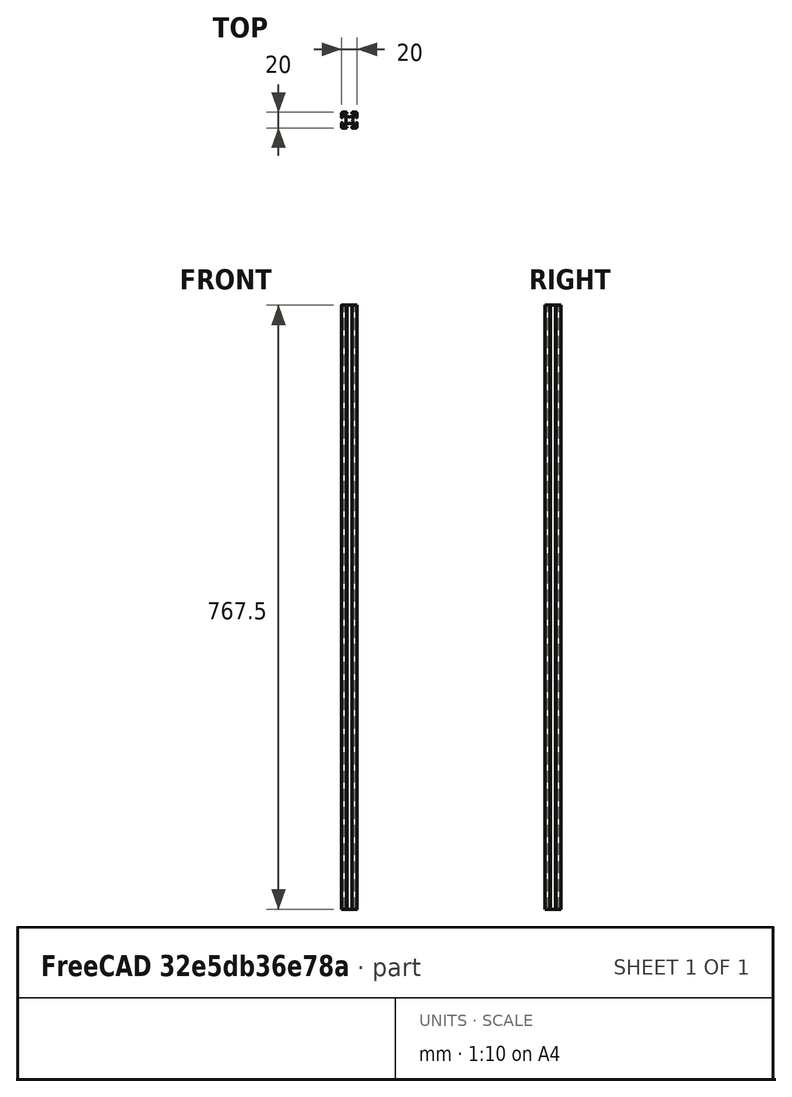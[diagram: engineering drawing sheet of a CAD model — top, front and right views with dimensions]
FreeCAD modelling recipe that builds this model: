
FCSTD DOCUMENT  (FreeCAD 0.15R4671 (Git))
Label: Perfil vertical 767.5 mm
License: CC-BY 3.0
LicenseURL: http://creativecommons.org/licenses/by/3.0/
objects: Sketcher::SketchObject×2, PartDesign::Pad×1, PartDesign::Pocket×1, Part::MultiFuse×1
note: 7 computed .brp shape members not serialized (recipe doc carries the construction recipe); baked Part::Feature solids carry a one-line shape summary decoded from their .brp

FEATURE [Sketcher::SketchObject] Sketch
  Placement = pos=(1.5,0,0) rot=(0,0,1;0rad)
  sketch-geometry (136):
    g0: LineSegment StartX=0 StartY=20 StartZ=0 EndX=4.65 EndY=20 EndZ=0
    g1: ArcOfCircle CenterX=-1e-12 CenterY=18.5 CenterZ=0 NormalX=0 NormalY=0 NormalZ=1 Radius=1.5 StartAngle=1.5708 EndAngle=3.14159
    g2: LineSegment StartX=-1.5 StartY=13.85 StartZ=0 EndX=-1.5 EndY=18.5 EndZ=0
    g3: ArcOfCircle CenterX=-1.3 CenterY=13.85 CenterZ=0 NormalX=0 NormalY=0 NormalZ=1 Radius=0.2 StartAngle=3.14159 EndAngle=4.71239
    g4: LineSegment StartX=-1 StartY=13.65 StartZ=0 EndX=-1.3 EndY=13.65 EndZ=0
    g5: LineSegment StartX=-1 StartY=13.3 StartZ=0 EndX=-1 EndY=13.65 EndZ=0
    g6: ArcOfCircle CenterX=-0.8 CenterY=13.3 CenterZ=0 NormalX=0 NormalY=0 NormalZ=1 Radius=0.2 StartAngle=3.14159 EndAngle=4.71239
    g7: LineSegment StartX=-0.5 StartY=13.1 StartZ=0 EndX=-0.8 EndY=13.1 EndZ=0
    g8: ArcOfCircle CenterX=-0.5 CenterY=13.6 CenterZ=0 NormalX=0 NormalY=0 NormalZ=1 Radius=0.5 StartAngle=4.71239 EndAngle=6.28319
    g9: LineSegment StartX=2.68e-07 StartY=15.5 StartZ=0 EndX=2.68e-07 EndY=13.6 EndZ=0
    g10: ArcOfCircle CenterX=0.5 CenterY=15.5 CenterZ=0 NormalX=0 NormalY=0 NormalZ=1 Radius=0.5 StartAngle=1.5708 EndAngle=3.14159
    g11: LineSegment StartX=1.23223 StartY=16 StartZ=0 EndX=0.5 EndY=16 EndZ=0
    g12: ArcOfCircle CenterX=1.23223 CenterY=15.5 CenterZ=0 NormalX=0 NormalY=0 NormalZ=1 Radius=0.5 StartAngle=0.785398 EndAngle=1.5708
    g13: LineSegment StartX=3.85355 StartY=13.5858 StartZ=0 EndX=1.58579 EndY=15.8536 EndZ=0
    g14: ArcOfCircle CenterX=3.5 CenterY=13.2322 CenterZ=0 NormalX=0 NormalY=0 NormalZ=1 Radius=0.5 StartAngle=0 EndAngle=0.785398
    g15: LineSegment StartX=4 StartY=10.9536 StartZ=0 EndX=4 EndY=13.2322 EndZ=0
    g16: ArcOfCircle CenterX=4.2 CenterY=10.9536 CenterZ=0 NormalX=0 NormalY=0 NormalZ=1 Radius=0.2 StartAngle=3.14159 EndAngle=3.66519
    g17: LineSegment StartX=4.46188 StartY=10.1 StartZ=0 EndX=4.0268 EndY=10.8536 EndZ=0
    g18: ArcOfCircle CenterX=4.28868 CenterY=10 CenterZ=0 NormalX=0 NormalY=0 NormalZ=1 Radius=0.2 StartAngle=5.75959 EndAngle=6.80678
    g19: LineSegment StartX=4.0268 StartY=9.14641 StartZ=0 EndX=4.46188 EndY=9.9 EndZ=0
    g20: ArcOfCircle CenterX=4.2 CenterY=9.04641 CenterZ=0 NormalX=0 NormalY=0 NormalZ=1 Radius=0.2 StartAngle=2.61799 EndAngle=3.14159
    g21: LineSegment StartX=4 StartY=6.76777 StartZ=0 EndX=4 EndY=9.04641 EndZ=0
    g22: ArcOfCircle CenterX=3.5 CenterY=6.76777 CenterZ=0 NormalX=0 NormalY=0 NormalZ=1 Radius=0.5 StartAngle=5.49779 EndAngle=6.28319
    g23: LineSegment StartX=1.58579 StartY=4.14645 StartZ=0 EndX=3.85355 EndY=6.41421 EndZ=0
    g24: ArcOfCircle CenterX=1.23223 CenterY=4.5 CenterZ=0 NormalX=0 NormalY=0 NormalZ=1 Radius=0.5 StartAngle=4.71239 EndAngle=5.49779
    g25: LineSegment StartX=0.5 StartY=4 StartZ=0 EndX=1.23223 EndY=4 EndZ=0
    g26: ArcOfCircle CenterX=0.5 CenterY=4.5 CenterZ=0 NormalX=0 NormalY=0 NormalZ=1 Radius=0.5 StartAngle=3.14159 EndAngle=4.71239
    g27: LineSegment StartX=2.68e-07 StartY=6.4 StartZ=0 EndX=2.68e-07 EndY=4.5 EndZ=0
    g28: ArcOfCircle CenterX=-0.5 CenterY=6.4 CenterZ=0 NormalX=0 NormalY=0 NormalZ=1 Radius=0.5 StartAngle=0 EndAngle=1.5708
    g29: LineSegment StartX=-0.8 StartY=6.9 StartZ=0 EndX=-0.5 EndY=6.9 EndZ=0
    g30: ArcOfCircle CenterX=-0.8 CenterY=6.7 CenterZ=0 NormalX=0 NormalY=0 NormalZ=1 Radius=0.2 StartAngle=1.5708 EndAngle=3.14159
    g31: LineSegment StartX=-1 StartY=6.35 StartZ=0 EndX=-1 EndY=6.7 EndZ=0
    g32: LineSegment StartX=-1.3 StartY=6.35 StartZ=0 EndX=-1 EndY=6.35 EndZ=0
    g33: ArcOfCircle CenterX=-1.3 CenterY=6.15 CenterZ=0 NormalX=0 NormalY=0 NormalZ=1 Radius=0.2 StartAngle=1.5708 EndAngle=3.14159
    g34: LineSegment StartX=-1.5 StartY=1.5 StartZ=0 EndX=-1.5 EndY=6.15 EndZ=0
    g35: ArcOfCircle CenterX=0 CenterY=1.5 CenterZ=0 NormalX=0 NormalY=0 NormalZ=1 Radius=1.5 StartAngle=3.14159 EndAngle=4.71239
    g36: LineSegment StartX=4.65 StartY=1e-12 StartZ=0 EndX=0 EndY=0 EndZ=0
    g37: ArcOfCircle CenterX=4.65 CenterY=0.2 CenterZ=0 NormalX=0 NormalY=0 NormalZ=1 Radius=0.2 StartAngle=4.71239 EndAngle=6.28319
    g38: LineSegment StartX=4.85 StartY=0.5 StartZ=0 EndX=4.85 EndY=0.2 EndZ=0
    g39: LineSegment StartX=5.2 StartY=0.5 StartZ=0 EndX=4.85 EndY=0.5 EndZ=0
    g40: ArcOfCircle CenterX=5.2 CenterY=0.7 CenterZ=0 NormalX=0 NormalY=0 NormalZ=1 Radius=0.2 StartAngle=4.71239 EndAngle=6.28319
    g41: LineSegment StartX=5.4 StartY=1 StartZ=0 EndX=5.4 EndY=0.7 EndZ=0
    g42: ArcOfCircle CenterX=4.9 CenterY=1 CenterZ=0 NormalX=0 NormalY=0 NormalZ=1 Radius=0.5 StartAngle=0 EndAngle=1.5708
    g43: LineSegment StartX=3 StartY=1.5 StartZ=0 EndX=4.9 EndY=1.5 EndZ=0
    g44: ArcOfCircle CenterX=3 CenterY=2 CenterZ=0 NormalX=0 NormalY=0 NormalZ=1 Radius=0.5 StartAngle=3.14159 EndAngle=4.71239
    g45: LineSegment StartX=2.5 StartY=2.73223 StartZ=0 EndX=2.5 EndY=2 EndZ=0
    g46: ArcOfCircle CenterX=3 CenterY=2.73223 CenterZ=0 NormalX=0 NormalY=0 NormalZ=1 Radius=0.5 StartAngle=2.35619 EndAngle=3.14159
    g47: LineSegment StartX=4.91421 StartY=5.35355 StartZ=0 EndX=2.64645 EndY=3.08579 EndZ=0
    g48: ArcOfCircle CenterX=5.26777 CenterY=5 CenterZ=0 NormalX=0 NormalY=0 NormalZ=1 Radius=0.5 StartAngle=1.5708 EndAngle=2.35619
    g49: LineSegment StartX=7.54641 StartY=5.5 StartZ=0 EndX=5.26777 EndY=5.5 EndZ=0
    g50: ArcOfCircle CenterX=7.54641 CenterY=5.7 CenterZ=0 NormalX=0 NormalY=0 NormalZ=1 Radius=0.2 StartAngle=4.71239 EndAngle=5.23599
    g51: LineSegment StartX=8.4 StartY=5.96188 StartZ=0 EndX=7.64641 EndY=5.52679 EndZ=0
    g52: ArcOfCircle CenterX=8.5 CenterY=5.78868 CenterZ=0 NormalX=0 NormalY=0 NormalZ=1 Radius=0.2 StartAngle=1.0472 EndAngle=2.0944
    g53: LineSegment StartX=9.35359 StartY=5.52679 StartZ=0 EndX=8.6 EndY=5.96188 EndZ=0
    g54: ArcOfCircle CenterX=9.45359 CenterY=5.7 CenterZ=0 NormalX=0 NormalY=0 NormalZ=1 Radius=0.2 StartAngle=4.18879 EndAngle=4.71239
    g55: LineSegment StartX=11.7322 StartY=5.5 StartZ=0 EndX=9.45359 EndY=5.5 EndZ=0
    g56: ArcOfCircle CenterX=11.7322 CenterY=5 CenterZ=0 NormalX=0 NormalY=0 NormalZ=1 Radius=0.5 StartAngle=0.785398 EndAngle=1.5708
    g57: LineSegment StartX=14.3536 StartY=3.08579 StartZ=0 EndX=12.0858 EndY=5.35355 EndZ=0
    g58: ArcOfCircle CenterX=14 CenterY=2.73223 CenterZ=0 NormalX=0 NormalY=0 NormalZ=1 Radius=0.5 StartAngle=0 EndAngle=0.785398
    g59: LineSegment StartX=14.5 StartY=2 StartZ=0 EndX=14.5 EndY=2.73223 EndZ=0
    g60: ArcOfCircle CenterX=14 CenterY=2 CenterZ=0 NormalX=0 NormalY=0 NormalZ=1 Radius=0.5 StartAngle=4.71239 EndAngle=6.28319
    g61: LineSegment StartX=12.1 StartY=1.5 StartZ=0 EndX=14 EndY=1.5 EndZ=0
    g62: ArcOfCircle CenterX=12.1 CenterY=1 CenterZ=0 NormalX=0 NormalY=0 NormalZ=1 Radius=0.5 StartAngle=1.5708 EndAngle=3.14159
    g63: LineSegment StartX=11.6 StartY=0.7 StartZ=0 EndX=11.6 EndY=1 EndZ=0
    g64: ArcOfCircle CenterX=11.8 CenterY=0.7 CenterZ=0 NormalX=0 NormalY=0 NormalZ=1 Radius=0.2 StartAngle=3.14159 EndAngle=4.71239
    g65: LineSegment StartX=12.15 StartY=0.5 StartZ=0 EndX=11.8 EndY=0.5 EndZ=0
    g66: LineSegment StartX=12.15 StartY=0.2 StartZ=0 EndX=12.15 EndY=0.5 EndZ=0
    g67: ArcOfCircle CenterX=12.35 CenterY=0.2 CenterZ=0 NormalX=0 NormalY=0 NormalZ=1 Radius=0.2 StartAngle=3.14159 EndAngle=4.71239
    g68: LineSegment StartX=17 StartY=1e-12 StartZ=0 EndX=12.35 EndY=0 EndZ=0
    g69: ArcOfCircle CenterX=17 CenterY=1.5 CenterZ=0 NormalX=0 NormalY=0 NormalZ=1 Radius=1.5 StartAngle=4.71239 EndAngle=6.28319
    g70: LineSegment StartX=18.5 StartY=6.15 StartZ=0 EndX=18.5 EndY=1.5 EndZ=0
    g71: ArcOfCircle CenterX=18.3 CenterY=6.15 CenterZ=0 NormalX=0 NormalY=0 NormalZ=1 Radius=0.2 StartAngle=0 EndAngle=1.5708
    g72: LineSegment StartX=18 StartY=6.35 StartZ=0 EndX=18.3 EndY=6.35 EndZ=0
    g73: LineSegment StartX=18 StartY=6.7 StartZ=0 EndX=18 EndY=6.35 EndZ=0
    g74: ArcOfCircle CenterX=17.8 CenterY=6.7 CenterZ=0 NormalX=0 NormalY=0 NormalZ=1 Radius=0.2 StartAngle=0 EndAngle=1.5708
    g75: LineSegment StartX=17.5 StartY=6.9 StartZ=0 EndX=17.8 EndY=6.9 EndZ=0
    g76: ArcOfCircle CenterX=17.5 CenterY=6.4 CenterZ=0 NormalX=0 NormalY=0 NormalZ=1 Radius=0.5 StartAngle=1.5708 EndAngle=3.14159
    g77: LineSegment StartX=17 StartY=4.5 StartZ=0 EndX=17 EndY=6.4 EndZ=0
    g78: ArcOfCircle CenterX=16.5 CenterY=4.5 CenterZ=0 NormalX=0 NormalY=0 NormalZ=1 Radius=0.5 StartAngle=4.71239 EndAngle=6.28319
    g79: LineSegment StartX=15.7678 StartY=4 StartZ=0 EndX=16.5 EndY=4 EndZ=0
    g80: ArcOfCircle CenterX=15.7678 CenterY=4.5 CenterZ=0 NormalX=0 NormalY=0 NormalZ=1 Radius=0.5 StartAngle=3.92699 EndAngle=4.71239
    g81: LineSegment StartX=13.1464 StartY=6.41421 StartZ=0 EndX=15.4142 EndY=4.14645 EndZ=0
    g82: ArcOfCircle CenterX=13.5 CenterY=6.76777 CenterZ=0 NormalX=0 NormalY=0 NormalZ=1 Radius=0.5 StartAngle=3.14159 EndAngle=3.92699
    g83: LineSegment StartX=13 StartY=9.04641 StartZ=0 EndX=13 EndY=6.76777 EndZ=0
    g84: ArcOfCircle CenterX=12.8 CenterY=9.04641 CenterZ=0 NormalX=0 NormalY=0 NormalZ=1 Radius=0.2 StartAngle=0 EndAngle=0.523599
    g85: LineSegment StartX=12.5381 StartY=9.9 StartZ=0 EndX=12.9732 EndY=9.14641 EndZ=0
    g86: ArcOfCircle CenterX=12.7113 CenterY=10 CenterZ=0 NormalX=0 NormalY=0 NormalZ=1 Radius=0.2 StartAngle=2.61799 EndAngle=3.66519
    g87: LineSegment StartX=12.9732 StartY=10.8536 StartZ=0 EndX=12.5381 EndY=10.1 EndZ=0
    g88: ArcOfCircle CenterX=12.8 CenterY=10.9536 CenterZ=0 NormalX=0 NormalY=0 NormalZ=1 Radius=0.2 StartAngle=5.75959 EndAngle=6.28319
    g89: LineSegment StartX=13 StartY=13.2322 StartZ=0 EndX=13 EndY=10.9536 EndZ=0
    g90: ArcOfCircle CenterX=13.5 CenterY=13.2322 CenterZ=0 NormalX=0 NormalY=0 NormalZ=1 Radius=0.5 StartAngle=2.35619 EndAngle=3.14159
    g91: LineSegment StartX=15.4142 StartY=15.8536 StartZ=0 EndX=13.1464 EndY=13.5858 EndZ=0
    g92: ArcOfCircle CenterX=15.7678 CenterY=15.5 CenterZ=0 NormalX=0 NormalY=0 NormalZ=1 Radius=0.5 StartAngle=1.5708 EndAngle=2.35619
    g93: LineSegment StartX=16.5 StartY=16 StartZ=0 EndX=15.7678 EndY=16 EndZ=0
    g94: ArcOfCircle CenterX=16.5 CenterY=15.5 CenterZ=0 NormalX=0 NormalY=0 NormalZ=1 Radius=0.5 StartAngle=0 EndAngle=1.5708
    g95: LineSegment StartX=17 StartY=13.6 StartZ=0 EndX=17 EndY=15.5 EndZ=0
    g96: ArcOfCircle CenterX=17.5 CenterY=13.6 CenterZ=0 NormalX=0 NormalY=0 NormalZ=1 Radius=0.5 StartAngle=3.14159 EndAngle=4.71239
    g97: LineSegment StartX=17.8 StartY=13.1 StartZ=0 EndX=17.5 EndY=13.1 EndZ=0
    g98: ArcOfCircle CenterX=17.8 CenterY=13.3 CenterZ=0 NormalX=0 NormalY=0 NormalZ=1 Radius=0.2 StartAngle=4.71239 EndAngle=6.28319
    g99: LineSegment StartX=18 StartY=13.65 StartZ=0 EndX=18 EndY=13.3 EndZ=0
    g100: LineSegment StartX=18.3 StartY=13.65 StartZ=0 EndX=18 EndY=13.65 EndZ=0
    g101: ArcOfCircle CenterX=18.3 CenterY=13.85 CenterZ=0 NormalX=0 NormalY=0 NormalZ=1 Radius=0.2 StartAngle=4.71239 EndAngle=6.28319
    g102: LineSegment StartX=18.5 StartY=18.5 StartZ=0 EndX=18.5 EndY=13.85 EndZ=0
    g103: ArcOfCircle CenterX=17 CenterY=18.5 CenterZ=0 NormalX=0 NormalY=0 NormalZ=1 Radius=1.5 StartAngle=0 EndAngle=1.5708
    g104: LineSegment StartX=12.35 StartY=20 StartZ=0 EndX=17 EndY=20 EndZ=0
    g105: ArcOfCircle CenterX=12.35 CenterY=19.8 CenterZ=0 NormalX=0 NormalY=0 NormalZ=1 Radius=0.2 StartAngle=1.5708 EndAngle=3.14159
    g106: LineSegment StartX=12.15 StartY=19.5 StartZ=0 EndX=12.15 EndY=19.8 EndZ=0
    g107: LineSegment StartX=11.8 StartY=19.5 StartZ=0 EndX=12.15 EndY=19.5 EndZ=0
    g108: ArcOfCircle CenterX=11.8 CenterY=19.3 CenterZ=0 NormalX=0 NormalY=0 NormalZ=1 Radius=0.2 StartAngle=1.5708 EndAngle=3.14159
    g109: LineSegment StartX=11.6 StartY=19 StartZ=0 EndX=11.6 EndY=19.3 EndZ=0
    g110: ArcOfCircle CenterX=12.1 CenterY=19 CenterZ=0 NormalX=0 NormalY=0 NormalZ=1 Radius=0.5 StartAngle=3.14159 EndAngle=4.71239
    g111: LineSegment StartX=14 StartY=18.5 StartZ=0 EndX=12.1 EndY=18.5 EndZ=0
    g112: ArcOfCircle CenterX=14 CenterY=18 CenterZ=0 NormalX=0 NormalY=0 NormalZ=1 Radius=0.5 StartAngle=0 EndAngle=1.5708
    g113: LineSegment StartX=14.5 StartY=17.2678 StartZ=0 EndX=14.5 EndY=18 EndZ=0
    g114: ArcOfCircle CenterX=14 CenterY=17.2678 CenterZ=0 NormalX=0 NormalY=0 NormalZ=1 Radius=0.5 StartAngle=5.49779 EndAngle=6.28319
    g115: LineSegment StartX=12.0858 StartY=14.6464 StartZ=0 EndX=14.3536 EndY=16.9142 EndZ=0
    g116: ArcOfCircle CenterX=11.7322 CenterY=15 CenterZ=0 NormalX=0 NormalY=0 NormalZ=1 Radius=0.5 StartAngle=4.71239 EndAngle=5.49779
    g117: LineSegment StartX=9.45359 StartY=14.5 StartZ=0 EndX=11.7322 EndY=14.5 EndZ=0
    g118: ArcOfCircle CenterX=9.45359 CenterY=14.3 CenterZ=0 NormalX=0 NormalY=0 NormalZ=1 Radius=0.2 StartAngle=1.5708 EndAngle=2.0944
    g119: LineSegment StartX=8.6 StartY=14.0381 StartZ=0 EndX=9.35359 EndY=14.4732 EndZ=0
    g120: ArcOfCircle CenterX=8.5 CenterY=14.2113 CenterZ=0 NormalX=0 NormalY=0 NormalZ=1 Radius=0.2 StartAngle=4.18879 EndAngle=5.23599
    g121: LineSegment StartX=7.64641 StartY=14.4732 StartZ=0 EndX=8.4 EndY=14.0381 EndZ=0
    g122: ArcOfCircle CenterX=7.54641 CenterY=14.3 CenterZ=0 NormalX=0 NormalY=0 NormalZ=1 Radius=0.2 StartAngle=1.0472 EndAngle=1.5708
    g123: LineSegment StartX=5.26777 StartY=14.5 StartZ=0 EndX=7.54641 EndY=14.5 EndZ=0
    g124: ArcOfCircle CenterX=5.26777 CenterY=15 CenterZ=0 NormalX=0 NormalY=0 NormalZ=1 Radius=0.5 StartAngle=3.92699 EndAngle=4.71239
    g125: LineSegment StartX=2.64645 StartY=16.9142 StartZ=0 EndX=4.91421 EndY=14.6464 EndZ=0
    g126: ArcOfCircle CenterX=3 CenterY=17.2678 CenterZ=0 NormalX=0 NormalY=0 NormalZ=1 Radius=0.5 StartAngle=3.14159 EndAngle=3.92699
    g127: LineSegment StartX=2.5 StartY=18 StartZ=0 EndX=2.5 EndY=17.2678 EndZ=0
    g128: ArcOfCircle CenterX=3 CenterY=18 CenterZ=0 NormalX=0 NormalY=0 NormalZ=1 Radius=0.5 StartAngle=1.5708 EndAngle=3.14159
    g129: LineSegment StartX=4.9 StartY=18.5 StartZ=0 EndX=3 EndY=18.5 EndZ=0
    g130: ArcOfCircle CenterX=4.9 CenterY=19 CenterZ=0 NormalX=0 NormalY=0 NormalZ=1 Radius=0.5 StartAngle=4.71239 EndAngle=6.28319
    g131: LineSegment StartX=5.4 StartY=19.3 StartZ=0 EndX=5.4 EndY=19 EndZ=0
    g132: ArcOfCircle CenterX=5.2 CenterY=19.3 CenterZ=0 NormalX=0 NormalY=0 NormalZ=1 Radius=0.2 StartAngle=0 EndAngle=1.5708
    g133: LineSegment StartX=4.85 StartY=19.5 StartZ=0 EndX=5.2 EndY=19.5 EndZ=0
    g134: LineSegment StartX=4.85 StartY=19.8 StartZ=0 EndX=4.85 EndY=19.5 EndZ=0
    g135: ArcOfCircle CenterX=4.65 CenterY=19.8 CenterZ=0 NormalX=0 NormalY=0 NormalZ=1 Radius=0.2 StartAngle=0 EndAngle=1.5708
  constraints (136):
    c: Coincident(g0,g1)
    c: Coincident(g135,g0)
    c: Coincident(g1,g2)
    c: Coincident(g2,g3)
    c: Coincident(g3,g4)
    c: Coincident(g4,g5)
    c: Coincident(g6,g5)
    c: Coincident(g7,g6)
    c: Coincident(g8,g7)
    c: Coincident(g9,g8)
    c: Coincident(g10,g9)
    c: Coincident(g10,g11)
    c: Coincident(g11,g12)
    c: Coincident(g12,g13)
    c: Coincident(g14,g13)
    c: Coincident(g15,g14)
    c: Coincident(g15,g16)
    c: Coincident(g16,g17)
    c: Coincident(g17,g18)
    c: Coincident(g18,g19)
    c: Coincident(g19,g20)
    c: Coincident(g20,g21)
    c: Coincident(g21,g22)
    c: Coincident(g22,g23)
    c: Coincident(g23,g24)
    c: Coincident(g24,g25)
    c: Coincident(g26,g25)
    c: Coincident(g26,g27)
    c: Coincident(g28,g27)
    c: Coincident(g28,g29)
    c: Coincident(g30,g29)
    c: Coincident(g31,g30)
    c: Coincident(g31,g32)
    c: Coincident(g32,g33)
    c: Coincident(g33,g34)
    c: Coincident(g35,g34)
    c: Coincident(g36,g35)
    c: Coincident(g37,g36)
    c: Coincident(g37,g38)
    c: Coincident(g38,g39)
    c: Coincident(g40,g39)
    c: Coincident(g40,g41)
    c: Coincident(g41,g42)
    c: Coincident(g43,g42)
    c: Coincident(g44,g43)
    c: Coincident(g44,g45)
    c: Coincident(g45,g46)
    c: Coincident(g46,g47)
    c: Coincident(g47,g48)
    c: Coincident(g49,g48)
    c: Coincident(g49,g50)
    c: Coincident(g50,g51)
    c: Coincident(g51,g52)
    c: Coincident(g53,g52)
    c: Coincident(g54,g53)
    c: Coincident(g55,g54)
    c: Coincident(g56,g55)
    c: Coincident(g56,g57)
    c: Coincident(g58,g57)
    c: Coincident(g59,g58)
    c: Coincident(g60,g59)
    c: Coincident(g61,g60)
    c: Coincident(g62,g61)
    c: Coincident(g62,g63)
    c: Coincident(g64,g63)
    c: Coincident(g65,g64)
    c: Coincident(g66,g65)
    c: Coincident(g67,g66)
    c: Coincident(g67,g68)
    c: Coincident(g69,g68)
    c: Coincident(g70,g69)
    c: Coincident(g71,g70)
    c: Coincident(g72,g71)
    c: Coincident(g73,g72)
    c: Coincident(g73,g74)
    c: Coincident(g75,g74)
    c: Coincident(g76,g75)
    c: Coincident(g76,g77)
    c: Coincident(g77,g78)
    c: Coincident(g78,g79)
    c: Coincident(g80,g79)
    c: Coincident(g81,g80)
    c: Coincident(g81,g82)
    c: Coincident(g82,g83)
    c: Coincident(g83,g84)
    c: Coincident(g85,g84)
    c: Coincident(g86,g85)
    c: Coincident(g86,g87)
    c: Coincident(g88,g87)
    c: Coincident(g88,g89)
    c: Coincident(g89,g90)
    c: Coincident(g91,g90)
    c: Coincident(g92,g91)
    c: Coincident(g93,g92)
    c: Coincident(g94,g93)
    c: Coincident(g94,g95)
    c: Coincident(g95,g96)
    c: Coincident(g96,g97)
    c: Coincident(g98,g97)
    c: Coincident(g98,g99)
    c: Coincident(g100,g99)
    c: Coincident(g100,g101)
    c: Coincident(g101,g102)
    c: Coincident(g102,g103)
    c: Coincident(g103,g104)
    c: Coincident(g104,g105)
    c: Coincident(g106,g105)
    c: Coincident(g107,g106)
    c: Coincident(g108,g107)
    c: Coincident(g109,g108)
    c: Coincident(g110,g109)
    c: Coincident(g111,g110)
    c: Coincident(g112,g111)
    c: Coincident(g112,g113)
    c: Coincident(g113,g114)
    c: Coincident(g114,g115)
    c: Coincident(g115,g116)
    c: Coincident(g117,g116)
    c: Coincident(g118,g117)
    c: Coincident(g119,g118)
    c: Coincident(g119,g120)
    c: Coincident(g121,g120)
    c: Coincident(g121,g122)
    c: Coincident(g122,g123)
    c: Coincident(g124,g123)
    c: Coincident(g124,g125)
    c: Coincident(g126,g125)
    c: Coincident(g127,g126)
    c: Coincident(g128,g127)
    c: Coincident(g129,g128)
    c: Coincident(g130,g129)
    c: Coincident(g130,g131)
    c: Coincident(g131,g132)
    c: Coincident(g133,g132)
    c: Coincident(g134,g133)
    c: Coincident(g135,g134)
FEATURE [PartDesign::Pad] Pad
  Length = 767.5
  Length2 = 100
  Placement = pos=(1.5,0,0) rot=(0,0,1;0rad)
  Sketch = -> Sketch
  Type = 0
FEATURE [Sketcher::SketchObject] Sketch001
  Placement = pos=(1.5,0,767.5) rot=(0,0,1;0rad)
  Support = -> Pad [Face138]
  sketch-geometry (16):
    g0: ArcOfCircle CenterX=8.5 CenterY=10 CenterZ=0 NormalX=0 NormalY=0 NormalZ=1 Radius=3.54978 StartAngle=2.14023 EndAngle=2.57348
    g1: LineSegment StartX=6.5861 StartY=12.9896 StartZ=0 EndX=7.24181 EndY=12.4453 EndZ=0
    g2: ArcOfCircle CenterX=8.5 CenterY=10 CenterZ=0 NormalX=0 NormalY=0 NormalZ=1 Radius=2.75 StartAngle=1.09559 EndAngle=2.046
    g3: LineSegment StartX=9.75819 StartY=12.4453 StartZ=0 EndX=10.4139 EndY=12.9896 EndZ=0
    g4: ArcOfCircle CenterX=8.5 CenterY=10 CenterZ=0 NormalX=0 NormalY=0 NormalZ=1 Radius=3.54978 StartAngle=0.568112 EndAngle=1.00136
    g5: LineSegment StartX=11.4922 StartY=11.9099 StartZ=0 EndX=10.9453 EndY=11.2582 EndZ=0
    g6: ArcOfCircle CenterX=8.5 CenterY=10 CenterZ=0 NormalX=0 NormalY=0 NormalZ=1 Radius=2.75 StartAngle=5.80798 EndAngle=6.75839
    g7: LineSegment StartX=10.9453 StartY=8.74181 StartZ=0 EndX=11.4922 EndY=8.09007 EndZ=0
    g8: ArcOfCircle CenterX=8.5 CenterY=10 CenterZ=0 NormalX=0 NormalY=0 NormalZ=1 Radius=3.54978 StartAngle=5.28183 EndAngle=5.71507
    g9: LineSegment StartX=10.4139 StartY=7.01036 StartZ=0 EndX=9.75819 EndY=7.5547 EndZ=0
    g10: ArcOfCircle CenterX=8.5 CenterY=10 CenterZ=0 NormalX=0 NormalY=0 NormalZ=1 Radius=2.75 StartAngle=4.23718 EndAngle=5.1876
    g11: LineSegment StartX=7.24181 StartY=7.5547 StartZ=0 EndX=6.5861 EndY=7.01036 EndZ=0
    g12: ArcOfCircle CenterX=8.5 CenterY=10 CenterZ=0 NormalX=0 NormalY=0 NormalZ=1 Radius=3.54978 StartAngle=3.7097 EndAngle=4.14295
    g13: LineSegment StartX=5.50783 StartY=8.09007 StartZ=0 EndX=6.0547 EndY=8.74181 EndZ=0
    g14: ArcOfCircle CenterX=8.5 CenterY=10 CenterZ=0 NormalX=0 NormalY=0 NormalZ=1 Radius=2.75 StartAngle=2.66639 EndAngle=3.6168
    g15: LineSegment StartX=6.0547 StartY=11.2582 StartZ=0 EndX=5.50783 EndY=11.9099 EndZ=0
  constraints (16):
    c: Coincident(g0,g1)
    c: Coincident(g15,g0)
    c: Coincident(g1,g2)
    c: Coincident(g3,g2)
    c: Coincident(g4,g3)
    c: Coincident(g4,g5)
    c: Coincident(g6,g5)
    c: Coincident(g7,g6)
    c: Coincident(g8,g7)
    c: Coincident(g9,g8)
    c: Coincident(g10,g9)
    c: Coincident(g11,g10)
    c: Coincident(g12,g11)
    c: Coincident(g13,g12)
    c: Coincident(g14,g13)
    c: Coincident(g15,g14)
FEATURE [PartDesign::Pocket] Pocket
  Length = 5
  Placement = pos=(1.5,0,0) rot=(0,0,1;0rad)
  Sketch = -> Sketch001
  Type = 1
FEATURE [Part::MultiFuse] Fusion  label="Perfil vertical 767,5"
  Shapes = -> [Pad,Pocket]
